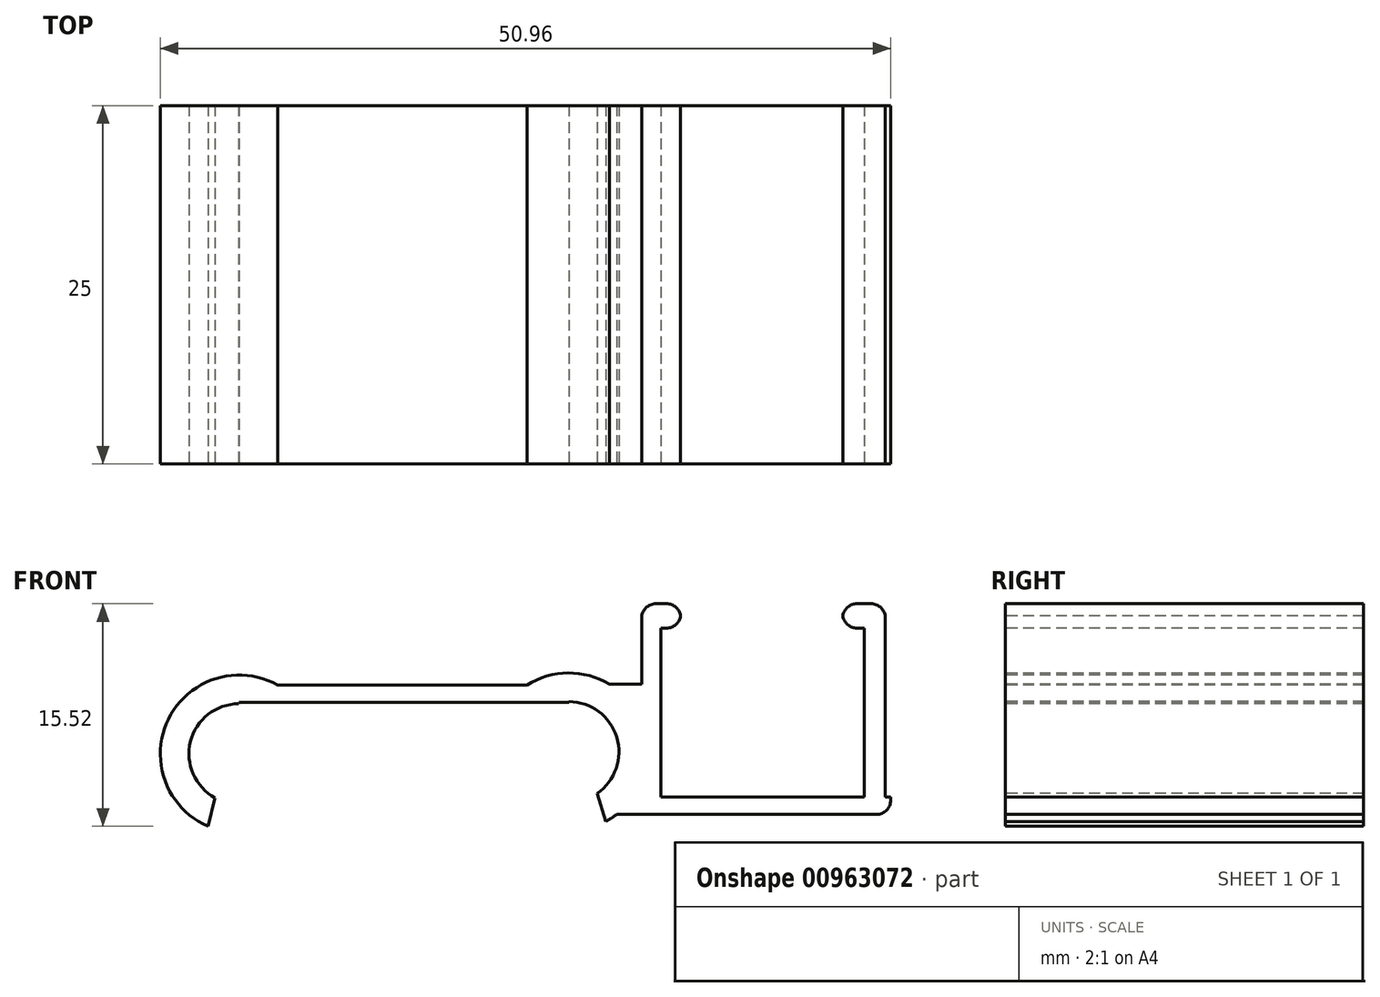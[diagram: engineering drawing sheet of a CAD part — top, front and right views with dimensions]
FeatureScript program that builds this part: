
annotation { "Feature Type Name" : "Feature", "Feature Type Description" : "" }
export const myFeature = defineFeature(function(context is Context, id is Id, definition is map)
    precondition{}
    {
        {
            var Q0;
            Q0=qCreatedBy(makeId("Top.planeOp"),FACE);
            var sketch = newSketch(context, id + "F0", { "sketchPlane" : qUnion([Q0])});
            skLineSegment(sketch, "E0.bottom", {"start": v(-11.5, 12.5) * mm, "end": v(11.5, 12.5) * mm});
            skLineSegment(sketch, "E0.top", {"start": v(-11.5, -12.5) * mm, "end": v(11.5, -12.5) * mm});
            skLineSegment(sketch, "E0.left", {"start": v(-11.5, 12.5) * mm, "end": v(-11.5, -12.5) * mm});
            skLineSegment(sketch, "E0.right", {"start": v(11.5, 12.5) * mm, "end": v(11.5, -12.5) * mm});
            skPoint(sketch, "E0.middle", {"position": v(0, 0) * mm});
            skSolve(sketch);
        }
        {
            var Q0;
            Q0=makeQuery(id+"F0.imprint","IMPRINT",FACE,{"disambiguationData":[TD([[makeQuery(id+"F0.imprint","IMPRINT",EDGE,{"derivedFrom":sQuery(id+"F0.wireOp",EDGE,"E0.bottom")}),-1.0]])]});
            extrude(context, id + "F1", {"entities" : qUnion([Q0]), "depth" : 1.2 * mm, "offsetDistance" : 25 * mm});
        }
        {
            var Q0;
            Q0=makeQuery(id+"F1.opExtrude","SWEPT_FACE",FACE,{"disambiguationData":[OSD([sQuery(id+"F0.wireOp",EDGE,"E0.top")])]});
            var sketch = newSketch(context, id + "F2", { "sketchPlane" : qUnion([Q0])});
            skLineSegment(sketch, "E1", {"start": v(11.5, 1.2) * mm, "end": v(11.5, -8.12) * mm, "construction": true});
            skCircle(sketch, "E2", {"center": v(-11.5, -3.6) * mm, "radius": 5.5 * mm});
            skCircle(sketch, "E3", {"center": v(11.5, -3.46) * mm, "radius": 5.5 * mm});
            skCircle(sketch, "E4", {"center": v(-11.5, -3.6) * mm, "radius": 3.5 * mm});
            skCircle(sketch, "E5", {"center": v(11.5, -3.46) * mm, "radius": 3.5 * mm});
            skLineSegment(sketch, "E6", {"start": v(-11.5, 0) * mm, "end": v(0, 0) * mm});
            skLineSegment(sketch, "E7", {"start": v(-14.98, -3.26) * mm, "end": v(15, -3.46) * mm, "construction": true});
            skLineSegment(sketch, "E8", {"start": v(-11.5, 0) * mm, "end": v(-16.46, -19.7) * mm});
            skLineSegment(sketch, "E9", {"start": v(11.5, 0) * mm, "end": v(20.16, -28) * mm});
            skSolve(sketch);
        }
        {
            var Q0;
            {var subQ0=sQuery(id+"F2.wireOp",EDGE,"E8");var subQ3=sQuery(id+"F2.wireOp",EDGE,"E4");var subQ7=makeQuery(id+"F2.imprint","INTERSECT",VERTEX,{"disambiguationData":[OD(0.0)],"derivedFrom":[subQ3,subQ0]});Q0=makeQuery(id+"F2.imprint","IMPRINT",FACE,{"disambiguationData":[TD([[makeQuery(id+"F2.imprint","IMPRINT",EDGE,{"disambiguationData":[TD([[subQ7,-1.0]])],"derivedFrom":subQ3}),-1.0]])]});}
            var Q1;
            {var subQ6=sQuery(id+"F2.wireOp",EDGE,"E9");var subQ8=sQuery(id+"F2.wireOp",EDGE,"E3");var subQ9=makeQuery(id+"F2.imprint","INTERSECT",VERTEX,{"derivedFrom":[subQ8,subQ6]});Q1=makeQuery(id+"F2.imprint","IMPRINT",FACE,{"disambiguationData":[TD([[makeQuery(id+"F2.imprint","IMPRINT",EDGE,{"disambiguationData":[TD([[subQ9,-1.0]])],"derivedFrom":subQ8}),1.0]])]});}
            extrude(context, id + "F3", {"entities" : qUnion([Q0, Q1]), "operationType" : NewBodyOperationType.ADD, "depth" : -25 * mm, "offsetDistance" : 25 * mm});
        }
        {
            var Q0;
            Q0=makeQuery(id+"F1.opExtrude","CAP_FACE",FACE,{"disambiguationData":[OSD([sQuery(id+"F0.wireOp",EDGE,"E0.bottom"),sQuery(id+"F0.wireOp",EDGE,"E0.top"),sQuery(id+"F0.wireOp",EDGE,"E0.left"),sQuery(id+"F0.wireOp",EDGE,"E0.right")])],"isStart":false});
            var sketch = newSketch(context, id + "F4", { "sketchPlane" : qUnion([Q0])});
            skLineSegment(sketch, "E10.bottom", {"start": v(-11, 10) * mm, "end": v(11, 10) * mm});
            skLineSegment(sketch, "E10.top", {"start": v(-11, -10) * mm, "end": v(11, -10) * mm});
            skLineSegment(sketch, "E10.left", {"start": v(-11, 10) * mm, "end": v(-11, -10) * mm});
            skLineSegment(sketch, "E10.right", {"start": v(11, 10) * mm, "end": v(11, -10) * mm});
            skPoint(sketch, "E10.middle", {"position": v(0, 0) * mm});
            skSolve(sketch);
        }
        {
            var Q0;
            {var subQ0=sQuery(id+"F0.wireOp",EDGE,"E0.top");Q0=makeQuery(id+"F3.boolean.opBoolean","MERGE",FACE,{"derivedFrom":[makeQuery(id+"F1.opExtrude","SWEPT_FACE",FACE,{"disambiguationData":[OSD([subQ0])]}),makeQuery(id+"F3.opExtrude","CAP_FACE",FACE,{"disambiguationData":[OSD([subQ0,sQuery(id+"F0.wireOp",EDGE,"E0.left"),sQuery(id+"F2.wireOp",EDGE,"E2"),sQuery(id+"F2.wireOp",EDGE,"E4"),sQuery(id+"F2.wireOp",EDGE,"E8")])],"isStart":true}),makeQuery(id+"F3.opExtrude","CAP_FACE",FACE,{"disambiguationData":[OSD([subQ0,sQuery(id+"F0.wireOp",EDGE,"E0.right"),sQuery(id+"F2.wireOp",EDGE,"E3"),sQuery(id+"F2.wireOp",EDGE,"E5"),sQuery(id+"F2.wireOp",EDGE,"E9")])],"isStart":true})]});}
            var sketch = newSketch(context, id + "F5", { "sketchPlane" : qUnion([Q0])});
            skLineSegment(sketch, "E11", {"start": v(0, 0) * mm, "end": v(0, 17.1) * mm, "construction": true});
            skLineSegment(sketch, "E12", {"start": v(16.59, -1.37) * mm, "end": v(16.59, 24.26) * mm, "construction": true});
            skLineSegment(sketch, "E13", {"start": v(16.59, -1.37) * mm, "end": v(16.59, -22.12) * mm, "construction": true});
            skLineSegment(sketch, "E14", {"start": v(16.59, -7.83) * mm, "end": v(33.96, -7.83) * mm});
            skLineSegment(sketch, "E15", {"start": v(33.96, -7.83) * mm, "end": v(33.96, -6.63) * mm});
            skLineSegment(sketch, "E16", {"start": v(33.96, -6.63) * mm, "end": v(16.59, -6.63) * mm});
            skLineSegment(sketch, "E17", {"start": v(16.59, -7.83) * mm, "end": v(14.85, -7.83) * mm});
            skLineSegment(sketch, "E18", {"start": v(16.59, -6.63) * mm, "end": v(16.59, -4.24) * mm});
            skLineSegment(sketch, "E19", {"start": v(16.59, -6.63) * mm, "end": v(16.59, 6.87) * mm});
            skLineSegment(sketch, "E20", {"start": v(16.59, 6.87) * mm, "end": v(33.59, 6.87) * mm, "construction": true});
            skLineSegment(sketch, "E21", {"start": v(33.59, 6.87) * mm, "end": v(33.59, -6.63) * mm});
            skLineSegment(sketch, "E22", {"start": v(17.92, 6.87) * mm, "end": v(17.92, -6.63) * mm});
            skLineSegment(sketch, "E23", {"start": v(32.12, 6.87) * mm, "end": v(32.12, -6.63) * mm});
            skLineSegment(sketch, "E24", {"start": v(17.92, 6.87) * mm, "end": v(16.59, 6.87) * mm});
            skLineSegment(sketch, "E25", {"start": v(32.12, 6.87) * mm, "end": v(33.59, 6.87) * mm});
            skLineSegment(sketch, "E26", {"start": v(17.92, -2.43) * mm, "end": v(32.12, -2.43) * mm, "construction": true});
            skPoint(sketch, "E26.startSnap0", {"position": v(14.85, -2.43) * mm});
            skLineSegment(sketch, "E27", {"start": v(17.92, 6.87) * mm, "end": v(19.32, 6.87) * mm, "construction": true});
            skLineSegment(sketch, "E28", {"start": v(19.32, 6.87) * mm, "end": v(19.32, 5.17) * mm});
            skLineSegment(sketch, "E29", {"start": v(19.32, 5.17) * mm, "end": v(17.92, 5.17) * mm});
            skLineSegment(sketch, "E30", {"start": v(32.12, 6.87) * mm, "end": v(30.6, 6.87) * mm});
            skLineSegment(sketch, "E31", {"start": v(30.6, 6.87) * mm, "end": v(30.6, 5.17) * mm});
            skLineSegment(sketch, "E32", {"start": v(30.6, 5.17) * mm, "end": v(32.12, 5.17) * mm});
            skLineSegment(sketch, "E33", {"start": v(17.92, 6.87) * mm, "end": v(19.32, 6.87) * mm});
            skLineSegment(sketch, "E34", {"start": v(18.62, 5.17) * mm, "end": v(18.62, -6.63) * mm, "construction": true});
            skLineSegment(sketch, "E35", {"start": v(31.37, 5.17) * mm, "end": v(31.37, -6.63) * mm, "construction": true});
            skLineSegment(sketch, "E36", {"start": v(14.33, 1.25) * mm, "end": v(16.59, 1.25) * mm});
            skPoint(sketch, "E36.endSnap0", {"position": v(16.59, 0.12) * mm});
            skSolve(sketch);
        }
        {
            var Q0;
            Q0=makeQuery(id+"F5.imprint","IMPRINT",FACE,{"disambiguationData":[TD([[makeQuery(id+"F5.imprint","IMPRINT",EDGE,{"derivedFrom":sQuery(id+"F5.wireOp",EDGE,"E28")}),-1.0]])]});
            var Q1;
            {var subQ8=sQuery(id+"F5.wireOp",EDGE,"E24");Q1=makeQuery(id+"F5.imprint","IMPRINT",FACE,{"disambiguationData":[TD([[makeQuery(id+"F5.imprint","IMPRINT",EDGE,{"derivedFrom":subQ8}),1.0]])]});}
            var Q2;
            {var subQ5=sQuery(id+"F5.wireOp",EDGE,"E21");Q2=makeQuery(id+"F5.imprint","IMPRINT",FACE,{"disambiguationData":[TD([[makeQuery(id+"F5.imprint","IMPRINT",EDGE,{"derivedFrom":subQ5}),-1.0]])]});}
            var Q3;
            {var subQ2=sQuery(id+"F5.wireOp",EDGE,"E30");Q3=makeQuery(id+"F5.imprint","IMPRINT",FACE,{"disambiguationData":[TD([[makeQuery(id+"F5.imprint","IMPRINT",EDGE,{"derivedFrom":subQ2}),1.0]])]});}
            var Q4;
            Q4=makeQuery(id+"F5.imprint","IMPRINT",FACE,{"disambiguationData":[TD([[makeQuery(id+"F5.imprint","IMPRINT",EDGE,{"derivedFrom":sQuery(id+"F5.wireOp",EDGE,"E14")}),1.0]])]});
            var Q5;
            {var subQ0=sQuery(id+"F5.wireOp",EDGE,"E36");Q5=makeQuery(id+"F5.imprint","IMPRINT",FACE,{"disambiguationData":[TD([[makeQuery(id+"F5.imprint","IMPRINT",EDGE,{"derivedFrom":subQ0}),-1.0]])]});}
            extrude(context, id + "F6", {"entities" : qUnion([Q0, Q1, Q2, Q3, Q4, Q5]), "operationType" : NewBodyOperationType.ADD, "depth" : -25 * mm, "offsetDistance" : 25 * mm});
        }
        {
            var Q0;
            Q0=makeQuery(id+"F6.opExtrude","SWEPT_EDGE",EDGE,{"disambiguationData":[OSD([sQuery(id+"F5.wireOp",EDGE,"E21"),sQuery(id+"F5.wireOp",EDGE,"E25")])]});
            var Q1;
            Q1=makeQuery(id+"F6.opExtrude","SWEPT_EDGE",EDGE,{"disambiguationData":[OSD([sQuery(id+"F5.wireOp",EDGE,"E19"),sQuery(id+"F5.wireOp",EDGE,"E24")])]});
            var Q2;
            Q2=makeQuery(id+"F6.opExtrude","SWEPT_EDGE",EDGE,{"disambiguationData":[OSD([sQuery(id+"F5.wireOp",EDGE,"E28"),sQuery(id+"F5.wireOp",EDGE,"E29")])]});
            var Q3;
            Q3=makeQuery(id+"F6.opExtrude","SWEPT_EDGE",EDGE,{"disambiguationData":[OSD([sQuery(id+"F5.wireOp",EDGE,"E31"),sQuery(id+"F5.wireOp",EDGE,"E32")])]});
            var Q4;
            Q4=makeQuery(id+"F6.opExtrude","SWEPT_EDGE",EDGE,{"disambiguationData":[OSD([sQuery(id+"F5.wireOp",EDGE,"E30"),sQuery(id+"F5.wireOp",EDGE,"E31")])]});
            var Q5;
            Q5=makeQuery(id+"F6.opExtrude","SWEPT_EDGE",EDGE,{"disambiguationData":[OSD([sQuery(id+"F5.wireOp",EDGE,"E28"),sQuery(id+"F5.wireOp",EDGE,"E33")])]});
            var Q6;
            Q6=makeQuery(id+"F6.opExtrude","SWEPT_EDGE",EDGE,{"disambiguationData":[OSD([sQuery(id+"F5.wireOp",EDGE,"E14"),sQuery(id+"F5.wireOp",EDGE,"E15")])]});
            fillet(context, id + "F7", {"entities" : qUnion([Q0, Q1, Q2, Q3, Q4, Q5, Q6]), "radius" : 1 * mm, "tangentPropagation" : true, "allowEdgeOverflow" : false});
        }
    });
